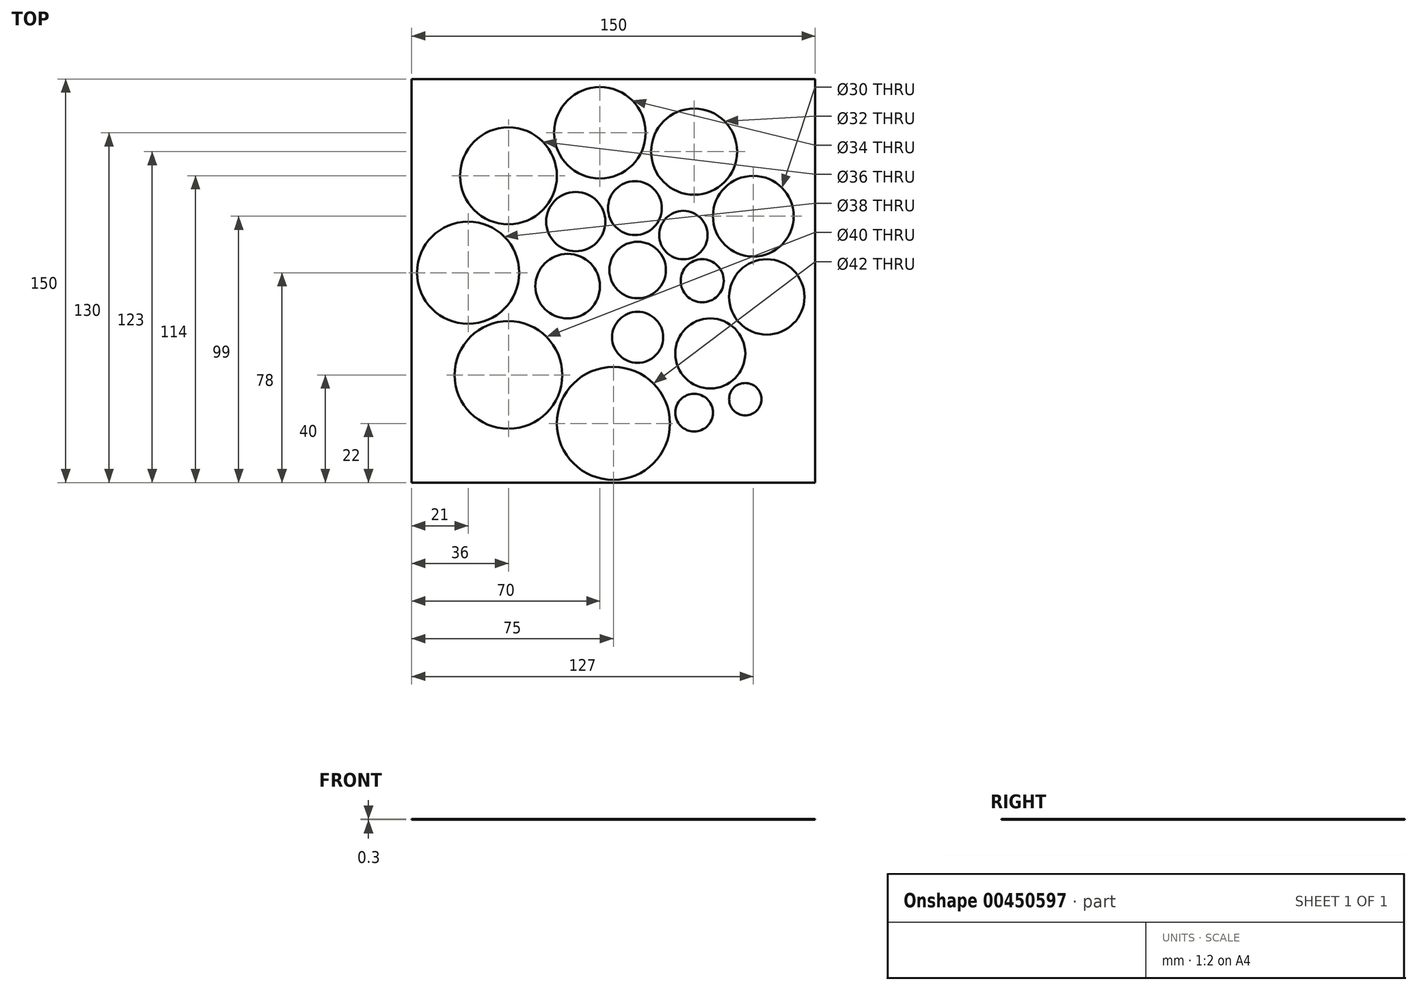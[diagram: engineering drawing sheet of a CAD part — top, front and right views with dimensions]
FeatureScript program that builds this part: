
annotation { "Feature Type Name" : "Feature", "Feature Type Description" : "" }
export const myFeature = defineFeature(function(context is Context, id is Id, definition is map)
    precondition{}
    {
        {
            var Q0;
            Q0=qCreatedBy(makeId("Top.planeOp"),FACE);
            var sketch = newSketch(context, id + "F0", { "sketchPlane" : qUnion([Q0])});
            skCircle(sketch, "E0", {"center": v(0, -53) * mm, "radius": 21 * mm});
            skCircle(sketch, "E1", {"center": v(-39, -35) * mm, "radius": 20 * mm});
            skCircle(sketch, "E2", {"center": v(-54, 3) * mm, "radius": 19 * mm});
            skCircle(sketch, "E3", {"center": v(-39, 39) * mm, "radius": 18 * mm});
            skCircle(sketch, "E4", {"center": v(-5, 55) * mm, "radius": 17 * mm});
            skCircle(sketch, "E5", {"center": v(30, 48) * mm, "radius": 16 * mm});
            skCircle(sketch, "E6", {"center": v(52, 24) * mm, "radius": 15 * mm});
            skCircle(sketch, "E7", {"center": v(57, -6) * mm, "radius": 14 * mm});
            skCircle(sketch, "E8", {"center": v(36, -27) * mm, "radius": 13 * mm});
            skCircle(sketch, "E9", {"center": v(-17, -2) * mm, "radius": 12 * mm});
            skCircle(sketch, "E10", {"center": v(-14, 22) * mm, "radius": 11 * mm});
            skCircle(sketch, "E11", {"center": v(8, 27) * mm, "radius": 10 * mm});
            skCircle(sketch, "E12", {"center": v(26, 17) * mm, "radius": 9 * mm});
            skCircle(sketch, "E13", {"center": v(33, 0) * mm, "radius": 8 * mm});
            skCircle(sketch, "E14", {"center": v(30, -49) * mm, "radius": 7 * mm});
            skCircle(sketch, "E15", {"center": v(49, -44) * mm, "radius": 6 * mm});
            skCircle(sketch, "E16", {"center": v(9, -21) * mm, "radius": 9.5 * mm});
            skCircle(sketch, "E17", {"center": v(9, 4) * mm, "radius": 10.5 * mm});
            skLineSegment(sketch, "E18.bottom", {"start": v(75, 75) * mm, "end": v(-75, 75) * mm});
            skLineSegment(sketch, "E18.top", {"start": v(75, -75) * mm, "end": v(-75, -75) * mm});
            skLineSegment(sketch, "E18.left", {"start": v(75, 75) * mm, "end": v(75, -75) * mm});
            skLineSegment(sketch, "E18.right", {"start": v(-75, 75) * mm, "end": v(-75, -75) * mm});
            skPoint(sketch, "E18.middle", {"position": v(0, 0) * mm});
            skSolve(sketch);
        }
        {
            var Q0;
            Q0 = qSketchRegion(id + "F0", true);
            extrude(context, id + "F1", {"entities" : qUnion([Q0]), "depth" : 0.3 * mm, "offsetDistance" : 25 * mm});
        }
    });
